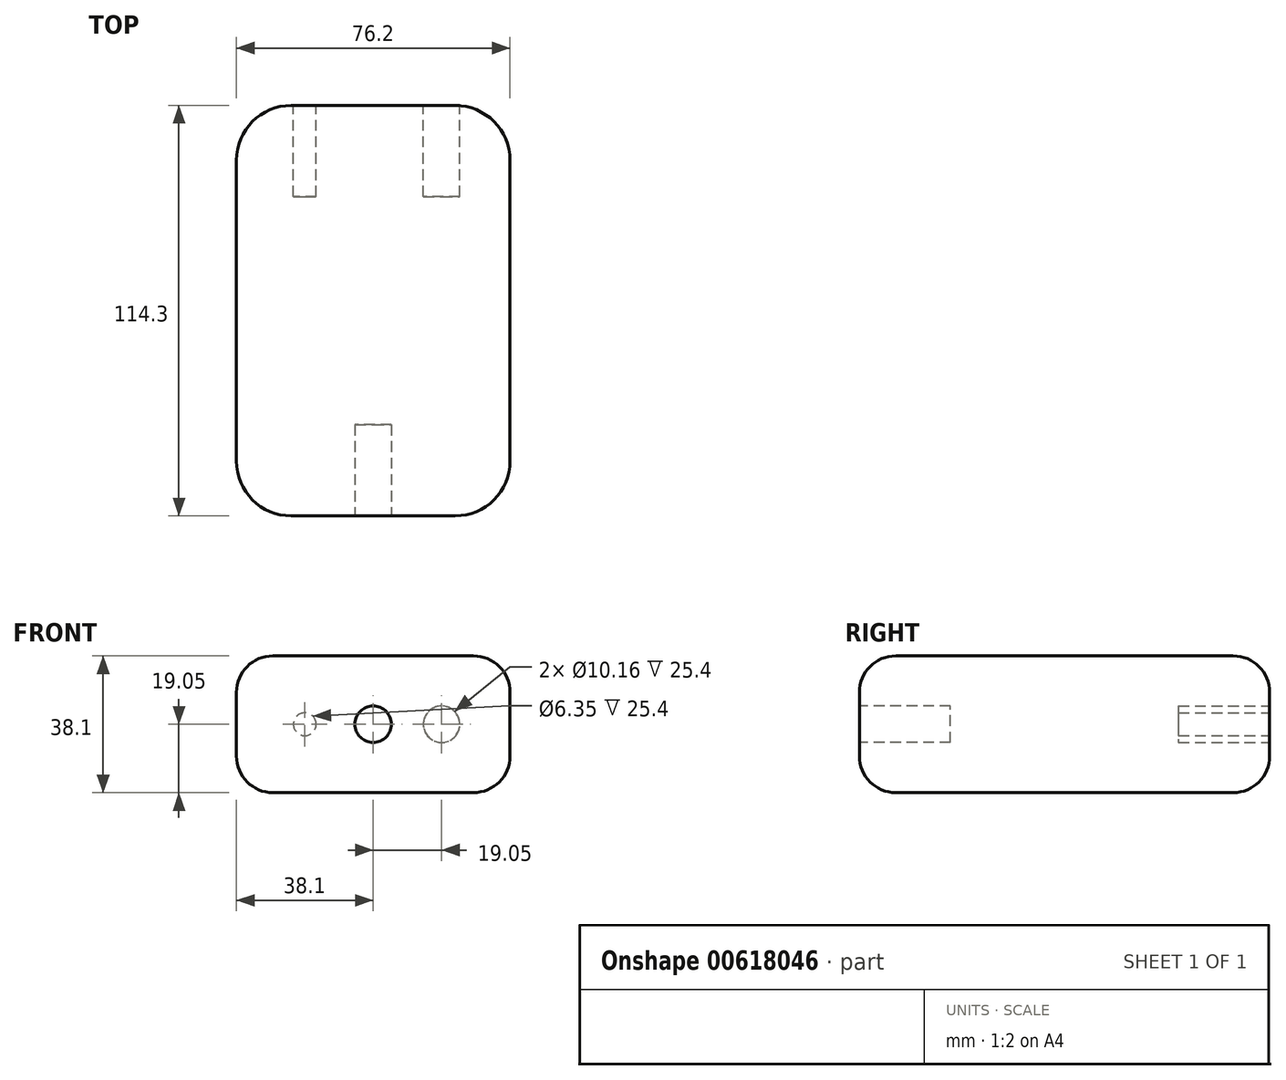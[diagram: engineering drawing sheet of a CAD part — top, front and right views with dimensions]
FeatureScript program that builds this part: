
annotation { "Feature Type Name" : "Feature", "Feature Type Description" : "" }
export const myFeature = defineFeature(function(context is Context, id is Id, definition is map)
    precondition{}
    {
        {
            var Q0;
            Q0=qCreatedBy(makeId("Top.planeOp"),FACE);
            var sketch = newSketch(context, id + "F0", { "sketchPlane" : qUnion([Q0])});
            skLineSegment(sketch, "E0.bottom", {"start": v(-22.86, 57.15) * mm, "end": v(22.86, 57.15) * mm});
            skLineSegment(sketch, "E0.top", {"start": v(-22.86, -57.15) * mm, "end": v(22.86, -57.15) * mm});
            skLineSegment(sketch, "E0.left", {"start": v(-38.1, 41.91) * mm, "end": v(-38.1, -41.91) * mm});
            skLineSegment(sketch, "E0.right", {"start": v(38.1, 41.91) * mm, "end": v(38.1, -41.91) * mm});
            skPoint(sketch, "E0.middle", {"position": v(0, 0) * mm});
            skPoint(sketch, "E1.visualSharp", {"position": v(-38.1, 57.15) * mm});
            skArc(sketch, "E1.filletArc", {"start": v(-22.86, 57.15) * mm, "mid": v(-33.64, 52.69) * mm, "end": v(-38.1, 41.91) * mm});
            skPoint(sketch, "E2.visualSharp", {"position": v(38.1, 57.15) * mm});
            skArc(sketch, "E2.filletArc", {"start": v(38.1, 41.91) * mm, "mid": v(33.64, 52.69) * mm, "end": v(22.86, 57.15) * mm});
            skPoint(sketch, "E3.visualSharp", {"position": v(-38.1, -57.15) * mm});
            skArc(sketch, "E3.filletArc", {"start": v(-38.1, -41.91) * mm, "mid": v(-33.64, -52.69) * mm, "end": v(-22.86, -57.15) * mm});
            skPoint(sketch, "E4.visualSharp", {"position": v(38.1, -57.15) * mm});
            skArc(sketch, "E4.filletArc", {"start": v(22.86, -57.15) * mm, "mid": v(33.64, -52.69) * mm, "end": v(38.1, -41.91) * mm});
            skSolve(sketch);
        }
        {
            var Q0;
            Q0 = qSketchRegion(id + "F0", true);
            extrude(context, id + "F1", {"entities" : qUnion([Q0]), "depth" : 38.1 * mm, "offsetDistance" : 25.4 * mm});
        }
        {
            var Q0;
            Q0=makeQuery(id+"F1.opExtrude","CAP_FACE",FACE,{"disambiguationData":[OSD([sQuery(id+"F0.wireOp",EDGE,"E0.bottom"),sQuery(id+"F0.wireOp",EDGE,"E0.top"),sQuery(id+"F0.wireOp",EDGE,"E0.left"),sQuery(id+"F0.wireOp",EDGE,"E0.right"),sQuery(id+"F0.wireOp",EDGE,"E1.filletArc"),sQuery(id+"F0.wireOp",EDGE,"E2.filletArc"),sQuery(id+"F0.wireOp",EDGE,"E3.filletArc"),sQuery(id+"F0.wireOp",EDGE,"E4.filletArc")])],"isStart":false});
            var Q1;
            Q1=makeQuery(id+"F1.opExtrude","CAP_FACE",FACE,{"disambiguationData":[OSD([sQuery(id+"F0.wireOp",EDGE,"E0.bottom"),sQuery(id+"F0.wireOp",EDGE,"E0.top"),sQuery(id+"F0.wireOp",EDGE,"E0.left"),sQuery(id+"F0.wireOp",EDGE,"E0.right"),sQuery(id+"F0.wireOp",EDGE,"E1.filletArc"),sQuery(id+"F0.wireOp",EDGE,"E2.filletArc"),sQuery(id+"F0.wireOp",EDGE,"E3.filletArc"),sQuery(id+"F0.wireOp",EDGE,"E4.filletArc")])],"isStart":true});
            fillet(context, id + "F2", {"entities" : qUnion([Q0, Q1]), "radius" : 10.16 * mm, "tangentPropagation" : true, "allowEdgeOverflow" : false});
        }
        {
            var Q0;
            Q0=makeQuery(id+"F1.opExtrude","SWEPT_FACE",FACE,{"disambiguationData":[OSD([sQuery(id+"F0.wireOp",EDGE,"E0.bottom")])]});
            var sketch = newSketch(context, id + "F3", { "sketchPlane" : qUnion([Q0])});
            skLineSegment(sketch, "E5", {"start": v(-22.86, 19.05) * mm, "end": v(22.86, 19.05) * mm, "construction": true});
            skCircle(sketch, "E6", {"center": v(-19.05, 19.05) * mm, "radius": 5.08 * mm});
            skCircle(sketch, "E7", {"center": v(19.05, 19.05) * mm, "radius": 3.18 * mm});
            skSolve(sketch);
        }
        {
            var Q0;
            Q0=makeQuery(id+"F1.opExtrude","SWEPT_FACE",FACE,{"disambiguationData":[OSD([sQuery(id+"F0.wireOp",EDGE,"E0.top")])]});
            var sketch = newSketch(context, id + "F4", { "sketchPlane" : qUnion([Q0])});
            skLineSegment(sketch, "E8", {"start": v(-22.86, 19.05) * mm, "end": v(22.86, 19.05) * mm, "construction": true});
            skCircle(sketch, "E9", {"center": v(0, 19.05) * mm, "radius": 5.08 * mm});
            skSolve(sketch);
        }
        {
            var Q0;
            Q0 = qSketchRegion(id + "F3", true);
            extrude(context, id + "F5", {"entities" : qUnion([Q0]), "operationType" : NewBodyOperationType.REMOVE, "oppositeDirection" : true, "depth" : 25.4 * mm, "offsetDistance" : 25.4 * mm});
        }
        {
            var Q0;
            Q0 = qSketchRegion(id + "F4", true);
            extrude(context, id + "F6", {"entities" : qUnion([Q0]), "operationType" : NewBodyOperationType.REMOVE, "oppositeDirection" : true, "depth" : 25.4 * mm, "offsetDistance" : 25.4 * mm});
        }
    });
